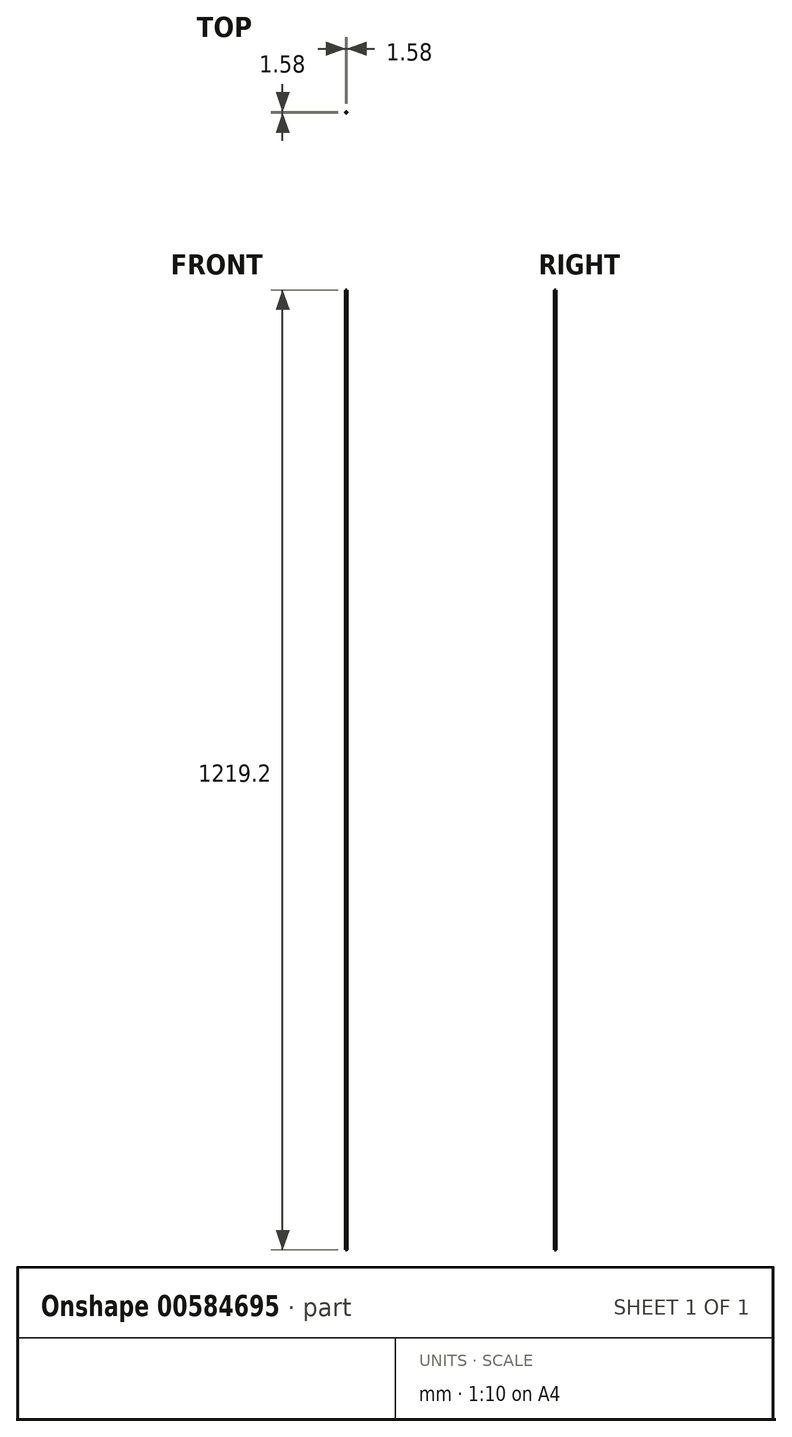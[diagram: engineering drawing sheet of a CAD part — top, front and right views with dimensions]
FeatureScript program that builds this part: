
annotation { "Feature Type Name" : "Feature", "Feature Type Description" : "" }
export const myFeature = defineFeature(function(context is Context, id is Id, definition is map)
    precondition{}
    {
        {
            var Q0;
            Q0=qCreatedBy(makeId("Top.planeOp"),FACE);
            var sketch = newSketch(context, id + "F0", { "sketchPlane" : qUnion([Q0])});
            skCircle(sketch, "E0", {"center": v(0, 0) * mm, "radius": 0.8 * mm});
            skSolve(sketch);
        }
        {
            var Q0;
            Q0 = qSketchRegion(id + "F0", true);
            extrude(context, id + "F1", {"entities" : qUnion([Q0]), "depth" : 1219.2 * mm, "offsetDistance" : 25 * mm});
        }
    });
